# Revit family: Table-Teknion-EMTF_With_Wood_Legs-R2016
name_source: partatom
category: Furniture
revit_build: Autodesk Revit 2018 (Build: 20190510_1515(x64)
units: mm (PartAtom-declared; Revit-internal decimal feet)

## family parameters
Always vertical = Yes
Cut with Voids When Loaded = No
OmniClass Number = 23.40.20.00
OmniClass Title = General Furniture and Specialties
Room Calculation Point = No
Shared = Yes
Work Plane-Based = No

## types (4) — shared parameters
Assembly Code = E2020200
Manufacturer = Teknion
Manufacturer Fax = 416.661.4586
Part Number = EMTF
Product Documentation Link = https://assets.teknion.com
Product Line = Emote
Product Page URL = https://www.teknion.com
Series = Emote
Sustainability Data = https://www.teknion.com
URL = www.teknion.com
Unit Weight URL = http://www.teknion.com
Warranty = http://www.teknion.com

## per-type parameters (varying)
| type | Description | Eased Corner, Square Edge Cut-Out | Eased Corners, Knife Edge Offset | Model | Rectangular Top, Knife Edge Offset |
| Rectangular Top, Square Edge | Table with Wood Legs, Rectangular Top, Square Edge | 1 " | 2.5 " | EMTFR___ | 2.5 " |
| Eased Corners, Square Edge | Table with Wood Legs, Eased Corners, Square Edge | 2.121 " | 2.5 " | EMTFE___ | 2.5 " |
| Rectangular Top, Knife Edge | Table with Wood Legs, Rectangular Top, Knife Edge | 1 " | 2.5 " | EMTFK___ | 0 " |
| Eased Corners, Knife Edge | Table with Wood Legs, Eased Corners, Knife Edge | 2.121 " | 0 " | EMTFN___ | 2.5 " |

type visibility flags (boolean, named after types; folded from table):
- Rectangular Top, Square Edge: Yes: (none)
- Eased Corners, Square Edge: Yes: Eased Corners, Square Edge
- Rectangular Top, Knife Edge: Yes: Rectangular Top, Knife Edge
- Eased Corners, Knife Edge: Yes: Eased Corners, Knife Edge

## geometry (parser evidence)
native form markers: Blend x33
no freeform markers — native parametric forms only
